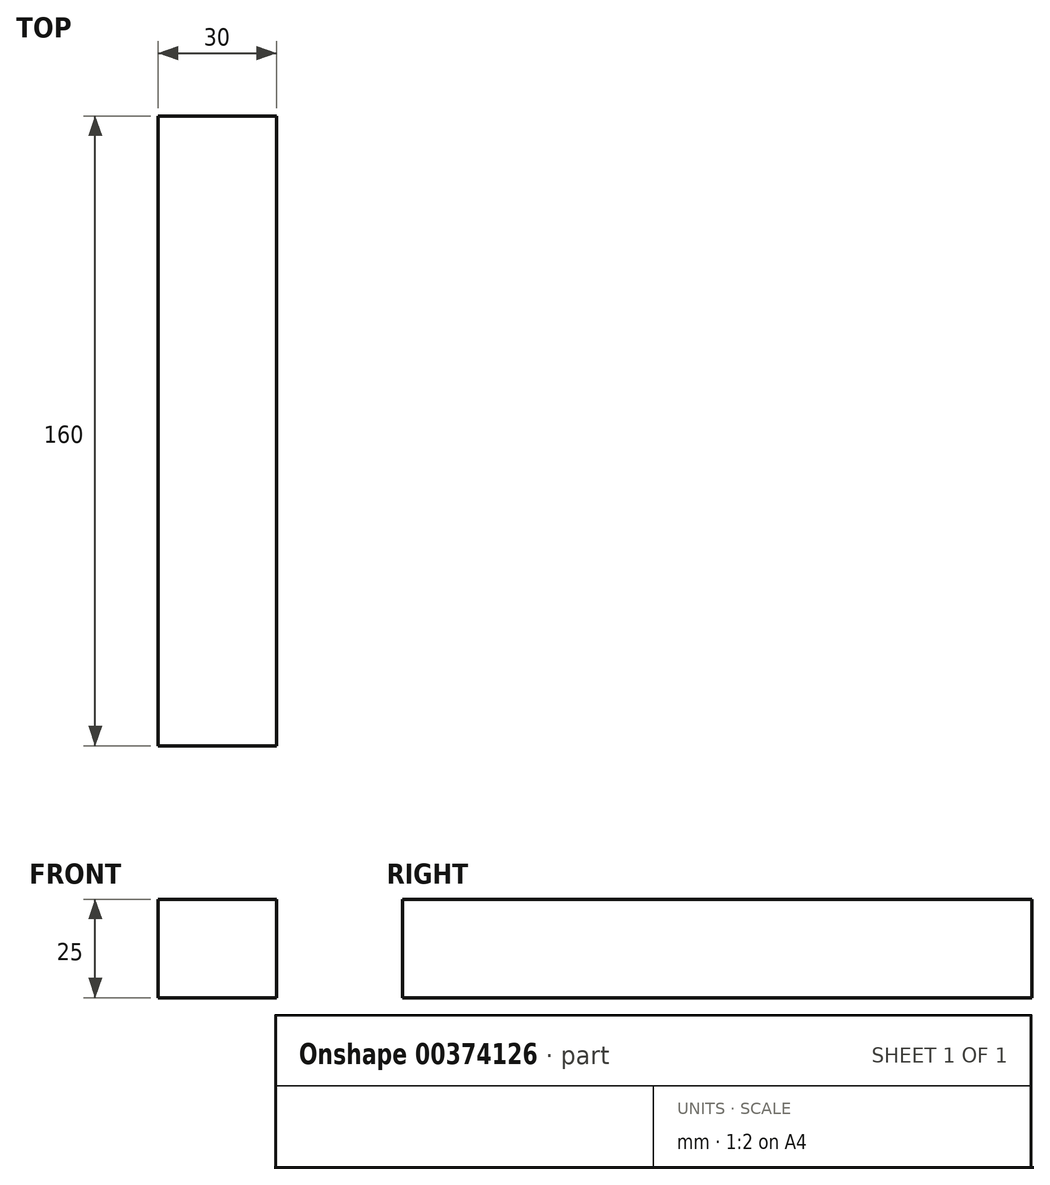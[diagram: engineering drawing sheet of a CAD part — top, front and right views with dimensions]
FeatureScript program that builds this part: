
annotation { "Feature Type Name" : "Feature", "Feature Type Description" : "" }
export const myFeature = defineFeature(function(context is Context, id is Id, definition is map)
    precondition{}
    {
        {
            var Q0;
            Q0=qCreatedBy(makeId("Top.planeOp"),FACE);
            var sketch = newSketch(context, id + "F0", { "sketchPlane" : qUnion([Q0])});
            skLineSegment(sketch, "E0.bottom", {"start": v(15, -80) * mm, "end": v(-15, -80) * mm});
            skLineSegment(sketch, "E0.top", {"start": v(15, 80) * mm, "end": v(-15, 80) * mm});
            skLineSegment(sketch, "E0.left", {"start": v(15, -80) * mm, "end": v(15, 80) * mm});
            skLineSegment(sketch, "E0.right", {"start": v(-15, -80) * mm, "end": v(-15, 80) * mm});
            skPoint(sketch, "E0.middle", {"position": v(0, 0) * mm});
            skSolve(sketch);
        }
        {
            var Q0;
            Q0 = qSketchRegion(id + "F0", true);
            extrude(context, id + "F1", {"entities" : qUnion([Q0]), "depth" : 25 * mm, "symmetric" : true});
        }
    });
